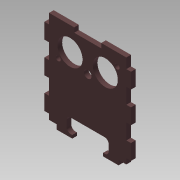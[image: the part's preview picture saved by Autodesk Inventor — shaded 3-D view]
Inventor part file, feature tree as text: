
AUTODESK INVENTOR PART (.ipt)
format: ipt  version: 2015 SP1 (Build 190203100, 203)  size: 161,792 bytes
history: native  units: mm
features: extrude x1, sketch x1
ambient origin geometry x8: Origin, YZ Plane, XZ Plane, XY Plane, X Axis, Y Axis, Z Axis, Center Point
bodies: Solid1 (feature_tree)
feature tree (2):
  extrude  "Extrusion1"  Depth=3.0mm
  sketch  "Sketch1"  dims[d0=10.0mm d1=3.0mm d2=20.0mm d4=15.0mm d5=20.0mm d7=15.0mm d14=10.0mm d15=90.0deg d16=20.0mm d18=20.0mm d19=20.0mm d21=20.0mm d24=3.0mm d25=0.0mm d26=3.0mm]
